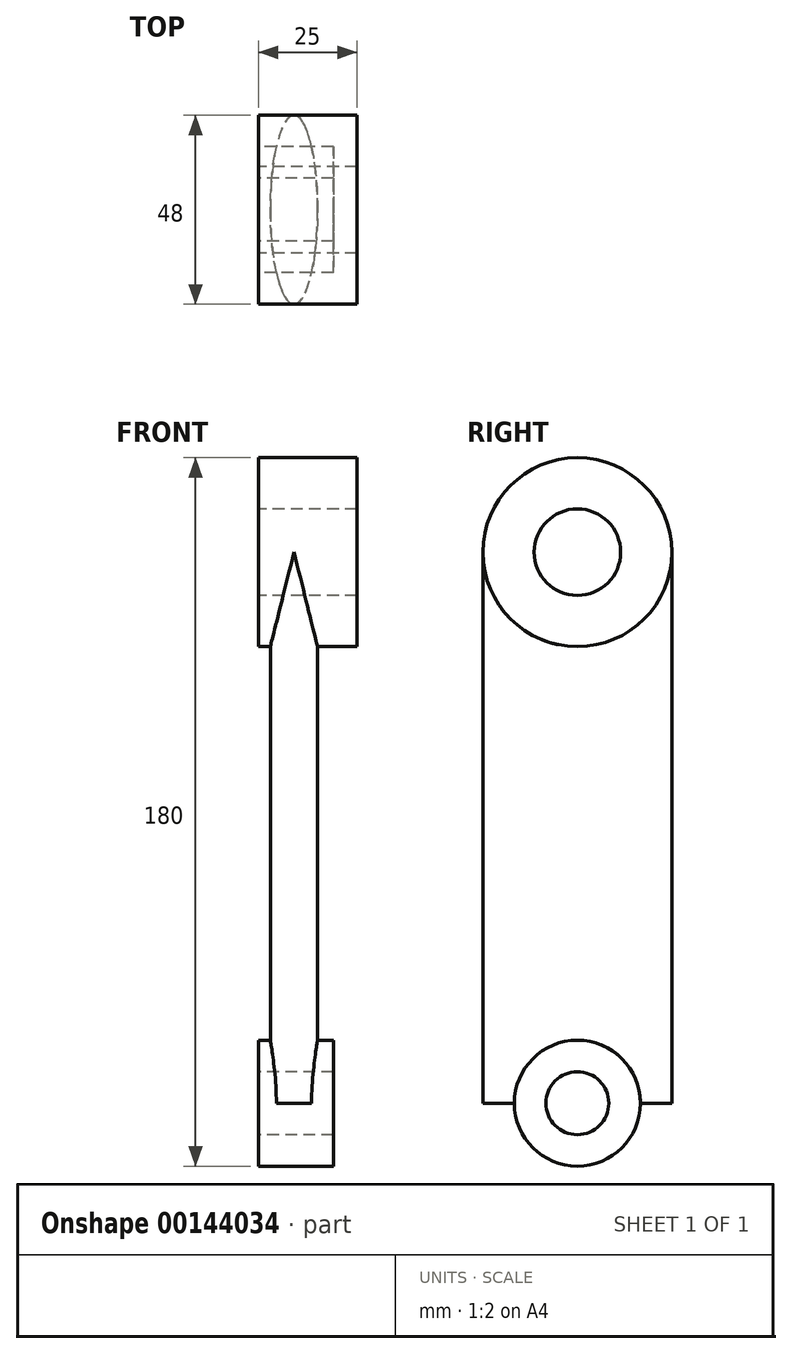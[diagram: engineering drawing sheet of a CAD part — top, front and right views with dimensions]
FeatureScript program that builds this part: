
annotation { "Feature Type Name" : "Feature", "Feature Type Description" : "" }
export const myFeature = defineFeature(function(context is Context, id is Id, definition is map)
    precondition{}
    {
        {
            var Q0;
            Q0=qCreatedBy(makeId("Right.planeOp"),FACE);
            var sketch = newSketch(context, id + "F0", { "sketchPlane" : qUnion([Q0])});
            skCircle(sketch, "E0", {"center": v(0, 0) * mm, "radius": 8 * mm});
            skCircle(sketch, "E1", {"center": v(0, 0) * mm, "radius": 16 * mm});
            skCircle(sketch, "E2", {"center": v(0, 140) * mm, "radius": 11 * mm});
            skCircle(sketch, "E3", {"center": v(0, 140) * mm, "radius": 24 * mm});
            skSolve(sketch);
        }
        {
            var Q0;
            Q0=makeQuery(id+"F0.imprint","IMPRINT",FACE,{"disambiguationData":[TD([[makeQuery(id+"F0.imprint","IMPRINT",EDGE,{"derivedFrom":sQuery(id+"F0.wireOp",EDGE,"E0")}),1.0]])]});
            var Q1;
            Q1=makeQuery(id+"F0.imprint","IMPRINT",FACE,{"disambiguationData":[TD([[makeQuery(id+"F0.imprint","IMPRINT",EDGE,{"derivedFrom":sQuery(id+"F0.wireOp",EDGE,"E0")}),-1.0]])]});
            extrude(context, id + "F1", {"entities" : qUnion([Q0, Q1]), "depth" : 19 * mm});
        }
        {
            var Q0;
            Q0=makeQuery(id+"F0.imprint","IMPRINT",FACE,{"disambiguationData":[TD([[makeQuery(id+"F0.imprint","IMPRINT",EDGE,{"derivedFrom":sQuery(id+"F0.wireOp",EDGE,"E2")}),1.0]])]});
            var Q1;
            Q1=makeQuery(id+"F0.imprint","IMPRINT",FACE,{"disambiguationData":[TD([[makeQuery(id+"F0.imprint","IMPRINT",EDGE,{"derivedFrom":sQuery(id+"F0.wireOp",EDGE,"E2")}),-1.0]])]});
            extrude(context, id + "F2", {"entities" : qUnion([Q0, Q1]), "depth" : 25 * mm});
        }
        {
            var Q0;
            Q0=qCreatedBy(makeId("Top.planeOp"),FACE);
            var sketch = newSketch(context, id + "F3", { "sketchPlane" : qUnion([Q0])});
            skEllipse(sketch, "E4", {"center": v(9, 0) * mm, "majorRadius": 24 * mm, "minorRadius": 6 * mm, "majorAxis": v(0, 1)});
            skPoint(sketch, "E5", {"position": v(3, 0) * mm});
            skLineSegment(sketch, "E6", {"start": v(0, 24) * mm, "end": v(25, 24) * mm, "construction": true});
            skSolve(sketch);
        }
        {
            var Q0;
            Q0=sQuery(id+"F0.wireOp",VERTEX,"E3.center");
            var Q1;
            Q1=qCreatedBy(makeId("Top.planeOp"),FACE);
            cPlane(context, id + "F4", {"entities" : qUnion([Q0, Q1]), "cplaneType" : CPlaneType.PLANE_POINT, "offset" : 25 * mm, "width" : 150 * mm, "height" : 150 * mm});
        }
        {
            var Q0;
            Q0=qCreatedBy(id+"F4.planeOp",FACE);
            var sketch = newSketch(context, id + "F5", { "sketchPlane" : qUnion([Q0])});
            skEllipse(sketch, "E7", {"center": v(9, 0) * mm, "majorRadius": 24 * mm, "minorRadius": 6 * mm, "majorAxis": v(0, 1)});
            skPoint(sketch, "E8", {"position": v(3, 0) * mm});
            skLineSegment(sketch, "E9", {"start": v(0, 24) * mm, "end": v(25, 24) * mm, "construction": true});
            skSolve(sketch);
        }
        {
            var Q0;
            Q0=makeQuery(id+"F5.imprint","IMPRINT",FACE,{"disambiguationData":[TD([[makeQuery(id+"F5.imprint","IMPRINT",EDGE,{"derivedFrom":sQuery(id+"F5.wireOp",EDGE,"E7")}),1.0]])]});
            var Q1;
            Q1=makeQuery(id+"F3.imprint","IMPRINT",FACE,{"disambiguationData":[TD([[makeQuery(id+"F3.imprint","IMPRINT",EDGE,{"derivedFrom":sQuery(id+"F3.wireOp",EDGE,"E4")}),1.0]])]});
            loft(context, id + "F6", {"operationType" : NewBodyOperationType.ADD, "sheetProfilesArray" : [{ "sheetProfileEntities" : qUnion([Q0]) }, { "sheetProfileEntities" : qUnion([Q1]) }]});
        }
        {
            var Q0;
            Q0=makeQuery(id+"F0.imprint","IMPRINT",FACE,{"disambiguationData":[TD([[makeQuery(id+"F0.imprint","IMPRINT",EDGE,{"derivedFrom":sQuery(id+"F0.wireOp",EDGE,"E2")}),1.0]])]});
            var Q1;
            Q1=makeQuery(id+"F0.imprint","IMPRINT",FACE,{"disambiguationData":[TD([[makeQuery(id+"F0.imprint","IMPRINT",EDGE,{"derivedFrom":sQuery(id+"F0.wireOp",EDGE,"E0")}),1.0]])]});
            extrude(context, id + "F7", {"entities" : qUnion([Q0, Q1]), "operationType" : NewBodyOperationType.REMOVE, "endBound" : BoundingType.THROUGH_ALL, "depth" : 25 * mm});
        }
    });
